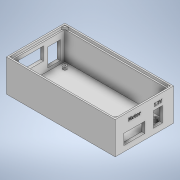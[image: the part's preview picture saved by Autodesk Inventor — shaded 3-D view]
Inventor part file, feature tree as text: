
AUTODESK INVENTOR PART (.ipt)
format: ipt  version: 2020 (Build 240168000, 168)  size: 593,408 bytes
history: native  units: mm
features: extrude x11, sketch x11, other x1
ambient origin geometry x8: Origin, YZ Plane, XZ Plane, XY Plane, X Axis, Y Axis, Z Axis, Center Point
bodies: Body1 (feature_tree)
feature tree (23):
  other  "Sólido1"
  extrude  "Extrusão1"  Depth=108.0mm
  extrude  "Extrusão2"  Depth=3.0mm
  extrude  "Extrusão3"  Depth=3.0mm
  extrude  "Extrusão4"  Depth=30.0mm TaperAngle=0.0deg
  extrude  "Extrusão5"  Depth=1.5mm
  extrude  "Extrusão6"  Depth=1.5mm
  extrude  "Extrusão8"  Depth=9.0mm
  extrude  "Extrusão9"  Depth=8.5mm
  extrude  "Extrusão10"  Depth=5.7mm
  extrude  "Extrusão12"  Depth=1.0mm TaperAngle=0.0deg
  extrude  "Extrusão13"  Depth=12.5mm
  sketch  "Esboço1"  dims[d0=58.0mm d1=108.0mm]
  sketch  "Esboço2"  dims[d2=32.0mm d3=0.0mm d4=3.0mm]
  sketch  "Esboço4"  dims[d5=102.0mm d6=3.0mm]
  sketch  "Esboço5"  dims[d7=52.0mm d8=30.0mm d9=0.0mm]
  sketch  "Esboço6"  dims[d10=1.5mm d11=1.5mm]
  sketch  "Esboço7"  dims[d12=1.5mm d13=1.5mm]
  sketch  "Esboço9"  dims[d14=2.5mm d15=0.0mm d17=9.0mm]
  sketch  "Esboço10"  dims[d20=20.7mm d23=8.5mm]
  sketch  "Esboço11"  dims[d24=8.1mm d25=5.7mm]
  sketch  "Esboço12"  dims[d26=5.0mm d27=0.0mm d29=1.0mm d30=0.0mm]
  sketch  "Esboço13"  dims[d31=4.5mm d32=12.5mm d33=6.0mm d34=25.0mm d35=13.0mm d36=11.0mm d37=5.0mm d38=0.0mm d39=18.0mm d48=1.0mm d49=0.0mm d50=0.0mm d51=0.8mm d52=0.0mm d53=0.8mm d54=0.0mm d55=3.75mm d56=15.0mm d57=3.5mm d58=10.5mm d59=3.0mm d60=1.6mm d61=6.0mm d62=6.0mm d63=1.6mm d64=1.6mm d65=1.6mm d66=6.0mm d67=6.0mm d68=6.0mm d69=6.0mm d70=6.0mm d71=6.0mm d72=4.0mm d73=4.0mm d74=4.0mm d75=4.0mm d78=2.5mm d79=0.0mm d80=2.0mm d81=0.0mm d16=0.5mm]
